# Revit family: Kessel AG 281200X en
name_source: partatom
category: Sanitärinstallationen
revit_build: Autodesk Revit 2014 (Build: 20130308_1515(x64)
units: mm (PartAtom-declared; Revit-internal decimal feet)

## types (1)
- Kessel AG 281200X en
    <1.010.00.2> Number of the part of the guideline = 4
    <1.010.00.3> Issue date (month) of the guideline = 201805
    <1.010.00.4> Manufacturer name = Kessel AG
    <1.010.00.5> Revision date of the file = 20190718
    <1.800.00.3> BS number = 00403000010000200200100100000100100100100000000014???
    <1.800.00.4> Comment field = Aqualift S Compact Mono, GTF 1200, Bodenplatte, befliesbar
    <1.810.00.3> Manufacturer’s reference number = 281200X
    <1.810.00.4> DATANORM number = 281200X
    <1.810.00.6> GTIN number = 4026092082614
    <1.960/3L.00.8> Link (URL) = http://www.kessel.de
    <4.100.00.4> Area of application = Entwässerung
    <4.110.00.4> Model series = Hebeanlage Aqualift S Compact
    <4.200.00.3> Design type = Pumpe freiaufgestellt
    <4.250.00.3> Shaft position = vertikal
    <4.260.00.3> Construction = Trockenläuferpumpe
    <4.300.00.3> Hydraulic = einstufig
    <4.350.00.3> Intake feature = normalansaugend
    <4.400.00.3> Actuator = E-Motor für Wechselstrom
    <4.450.00.3> Type of speed adjustment = keine
    <4.460.00.3> E-motor startup mode = direkt
    <4.500.00.3> Material specifications pump housing = Kunststoff, Edelstahl
    <4.700.00.10> Star / delta starting circuit with three-phase connection or three-phase current = no
    <4.700.00.11> Rated frequency [Hz] = 50
    <4.700.00.12> Degree of protection = IP 68
    <4.700.00.13> Heat class = F
    <4.700.00.15> Maximum temperature of pumped medium [°C] = 35
    <4.700.00.16> Minimum temperature of pumped medium [°C] = 0
    <4.700.00.21> Maximum working pressure Pmax PN [hPa] = 900
    <4.700.00.22> Maximum shaft output (P2) per pump/drive [W] = 0.84
    <4.700.00.23> Nominal speed n [1/min] = 2650
    <4.700.00.24> Maximum speed n [1/min] = 2650
    <4.700.00.25> minimum speed at int. speed adjustment [1/min] = 0
    <4.700.00.26> maximum power consumption per pump / drive [A] = 6.2
    <4.700.00.27> inrush current [A] = 14.9
    <4.700.00.28> Motor-pump shaft = durchgehend
    <4.700.00.29> shaft seal = RWDR
    <4.700.00.30> Total number of pumps / drives = 1
    <4.700.00.31> Number of operating pumps / drives = 1
    <4.700.00.32> Net mass [kg] = 17.47
    <4.700.00.33> electrical rating (P1) [W] = 1.4
    <4.700.00.34> maximum flow [m3/h] = 15.5
    <4.700.00.37> maximum delivery height [m] = 9
    <4.700.00.46> vertical installation = yes
    <4.700.00.47> outdoor installation = no
    <4.700.00.48> ATEX = no
    <4.700.00.49> protection class = protection class I
    <4.700.00.4> Product name = Aqualift S Compact Mono, GTF 1200, Bodenplatte, befliesbar
    <4.700.00.50> motor protection = no
    <4.700.00.6> Nominal connection size on pressure side = 32
    <4.700.00.7> Nominal connection size on suction side = 100
    <4.700.00.8> Electrical connection [V] = 230
    <4.700.00.9> Voltage = 1/N/PE 230V
    <4.710.01.10> Type of wastewater disposal plant = Single unit (mono)
    <4.710.01.11> Installation site of the plant = Underfloor (in the bottom plate)
    <4.710.01.13> Mass pump (net) [kg] = 10
    <4.710.01.14> Mass overall system (net) [kg] = 17.47
    <4.710.01.18> Backflow preventer available = yes
    <4.710.01.20> ATEX for switching device = no
    <4.710.01.21> Function switching device = without alarm message
    <4.710.01.28> Battery operation of the warning device possible = no
    <4.710.01.4> Deliverable volume between on and off volume of the collection container [l] = 16
    <4.710.01.5> Cutting device available = no
    <4.710.01.6> free ball passage [mm] = 30
    <4.710.01.7> operating mode = S3
    <4.710.01.8> Type of S2 / S3 operation = 50 %
    <4.710.01.9> Type of wastewater plant = Wastewater lifting plant for sewage-free wastewater (EN 12050-2)
    <4.710.02.10> Mass pump (net) [kg] = 10
    <4.710.02.3> free ball passage [mm] = 30
    <4.710.02.4> Attached pump control = yes
    <4.710.02.5> cutter = no
    <4.710.02.6> operating mode = S3
    <4.710.02.7> Type of S2 / S3 operation = 50 %
    <4.710.02.8> Application of the wastewater pump = Wastewater lifting plant for sewage-free wastewater (EN 12050-2)
    <4.710.02.9> Location of the pump = Underfloor (in the bottom plate)
    <4.710.03.3> Type of measurements = Dimensions
    <4.710.03.4> length [mm] = 620
    <4.710.03.5> width [mm] = 580
    <4.710.03.6> height [mm] = 490
    <4.710.03.7> Mass (net) [kg] = 17.47
    CONNECTOR0_DIAMETER_dX_0r = 0 mm  [stored 0 ft]
    CONNECTOR0_dX_00 = 326 mm
    CONNECTOR0_dX_01 = 266 mm
    CONNECTOR0_ref_dX = 266 mm
    CONNECTOR0_ref_dZ = 209 mm
    CONNECTOR1_DIAMETER_dZ_0r = 0 mm  [stored 0 ft]
    CONNECTOR1_dZ_00 = 426 mm
    CONNECTOR1_dZ_01 = 486 mm
    CONNECTOR1_ref_dZ = 426 mm
    CONNECTOR2_DIAMETER_dNBN0_0r = 0 mm  [stored 0 ft]
    CONNECTOR2_dNBN0_00 = 326 mm
    CONNECTOR2_dNBN0_01 = 331 mm
    CONNECTOR2_ref_dNBN0 = 326 mm
    CONNECTOR2_ref_dNBN1 = 10 mm  [stored 0.0328084 ft]
    CONNECTOR2_ref_dZ = 376 mm
    CONNECTOR3_DIAMETER_dNBN0_0r = 0 mm  [stored 0 ft]
    CONNECTOR3_dNBN0_00 = 326 mm
    CONNECTOR3_dNBN0_01 = 331 mm
    CONNECTOR3_ref_dNBN0 = 326 mm
    CONNECTOR3_ref_dNBN1 = 10 mm  [stored 0.0328084 ft]
    CONNECTOR3_ref_dZ = 364 mm
    CONNECTOR4_DIAMETER_dNBN0_0r = 0 mm  [stored 0 ft]
    CONNECTOR4_dNBN0_00 = 326 mm
    CONNECTOR4_dNBN0_01 = 331 mm
    CONNECTOR4_ref_dNBN0 = 326 mm
    CONNECTOR4_ref_dNBN1 = 10 mm  [stored 0.0328084 ft]
    CONNECTOR4_ref_dZ = 376 mm
    CONNECTOR5_DIAMETER_dNBN0_0r = 0 mm  [stored 0 ft]
    CONNECTOR5_dNBN0_00 = 326 mm
    CONNECTOR5_dNBN0_01 = 331 mm
    CONNECTOR5_ref_dNBN0 = 326 mm
    CONNECTOR5_ref_dNBN1 = 10 mm  [stored 0.0328084 ft]
    CONNECTOR5_ref_dZ = 364 mm
    CONNECTOR6_DIAMETER_dNBN0_0r = 0 mm  [stored 0 ft]
    CONNECTOR6_dNBN0_00 = 278 mm
    CONNECTOR6_dNBN0_01 = 268 mm
    CONNECTOR6_ref_dNBN0 = 268 mm
    CONNECTOR6_ref_dZ = 209 mm
    CONNECTOR7_DIAMETER_dNBN0_0r = 0 mm  [stored 0 ft]
    CONNECTOR7_dNBN0_00 = 268 mm
    CONNECTOR7_dNBN0_01 = 278 mm
    CONNECTOR7_ref_dNBN0 = 268 mm
    CONNECTOR7_ref_dZ = 209 mm
    CONNECTOR8_DIAMETER_dX_0r = 0 mm  [stored 0 ft]
    CONNECTOR8_dX_00 = 263 mm
    CONNECTOR8_dX_01 = 273 mm
    CONNECTOR8_ref_dNBN0 = 188 mm
    CONNECTOR8_ref_dNBN1 = 183 mm
    CONNECTOR8_ref_dZ = 363 mm
    CONNECTOR9_DIAMETER_dX_0r = 0 mm  [stored 0 ft]
    CONNECTOR9_dX_00 = 246 mm
    CONNECTOR9_dX_01 = 236 mm
    CONNECTOR9_ref_dNBN0 = 167 mm
    CONNECTOR9_ref_dNBN1 = 167 mm
    CONNECTOR9_ref_dZ = 370 mm
    Hersteller = Kessel AG
    Modell = 281200X
    URL = www.kessel.de

note: [stored X ft] marks values corroborated as IEEE doubles in the binary element streams (Revit-internal decimal feet)
